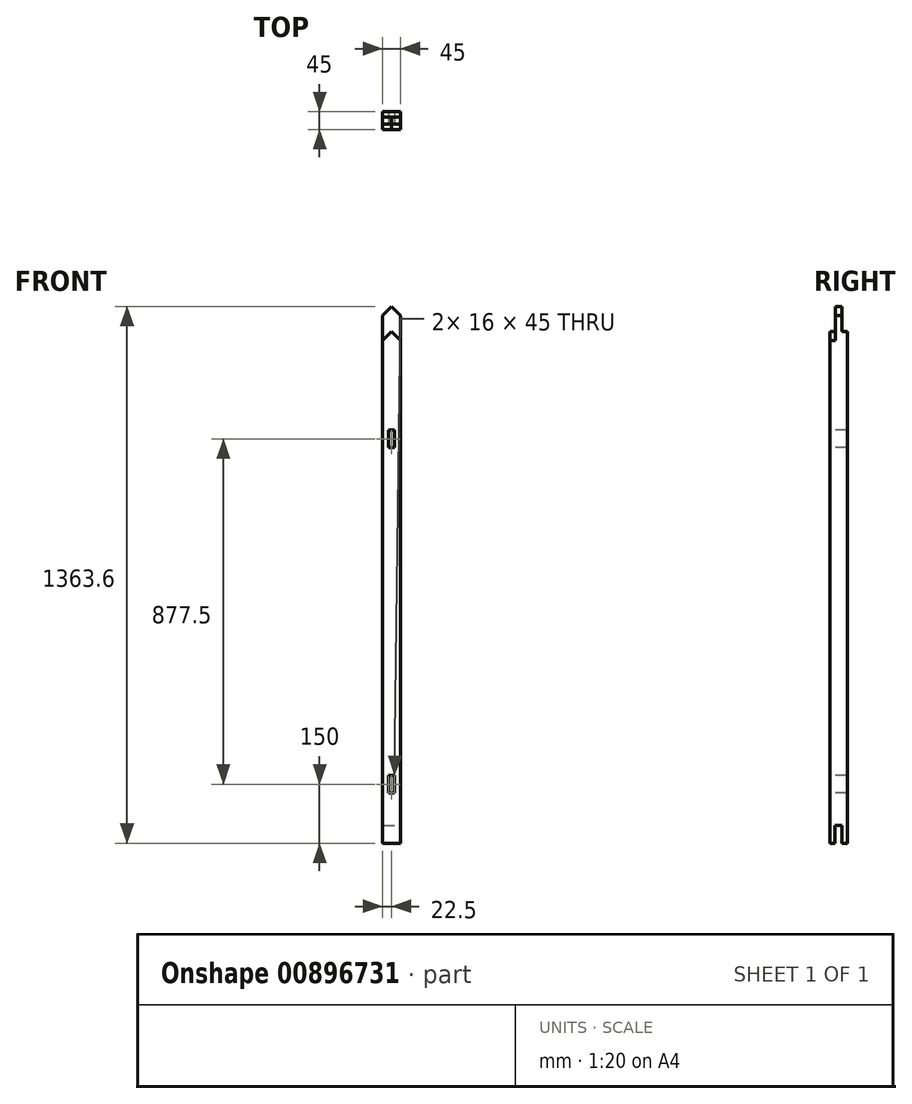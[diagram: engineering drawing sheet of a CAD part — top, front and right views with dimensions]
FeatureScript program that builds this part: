
annotation { "Feature Type Name" : "Feature", "Feature Type Description" : "" }
export const myFeature = defineFeature(function(context is Context, id is Id, definition is map)
    precondition{}
    {
        {
            var Q0;
            Q0=qCreatedBy(makeId("Top.planeOp"),FACE);
            var sketch = newSketch(context, id + "F0", { "sketchPlane" : qUnion([Q0])});
            skLineSegment(sketch, "E0.bottom", {"start": v(22.5, 22.5) * mm, "end": v(-22.5, 22.5) * mm});
            skLineSegment(sketch, "E0.top", {"start": v(22.5, -22.5) * mm, "end": v(-22.5, -22.5) * mm});
            skLineSegment(sketch, "E0.left", {"start": v(22.5, 22.5) * mm, "end": v(22.5, -22.5) * mm});
            skLineSegment(sketch, "E0.right", {"start": v(-22.5, 22.5) * mm, "end": v(-22.5, -22.5) * mm});
            skPoint(sketch, "E0.middle", {"position": v(0, 0) * mm});
            skSolve(sketch);
        }
        {
            var Q0;
            Q0 = qSketchRegion(id + "F0", true);
            extrude(context, id + "F1", {"entities" : qUnion([Q0]), "endBound" : BoundingType.SYMMETRIC, "depth" : 1300 * mm, "offsetDistance" : 25 * mm});
        }
        {
            var Q0;
            Q0=makeQuery(id+"F1.opExtrude","SWEPT_FACE",FACE,{"disambiguationData":[OSD([sQuery(id+"F0.wireOp",EDGE,"E0.top")])]});
            var sketch = newSketch(context, id + "F2", { "sketchPlane" : qUnion([Q0])});
            skLineSegment(sketch, "E1", {"start": v(0, 650) * mm, "end": v(22.5, 627.5) * mm});
            skLineSegment(sketch, "E2", {"start": v(22.5, 627.5) * mm, "end": v(22.5, 650) * mm});
            skLineSegment(sketch, "E3", {"start": v(22.5, 650) * mm, "end": v(0, 650) * mm});
            skLineSegment(sketch, "E4", {"start": v(0, 650) * mm, "end": v(-22.5, 627.5) * mm});
            skLineSegment(sketch, "E5", {"start": v(-22.5, 627.5) * mm, "end": v(-22.5, 650) * mm});
            skLineSegment(sketch, "E6", {"start": v(-22.5, 650) * mm, "end": v(0, 650) * mm});
            skSolve(sketch);
        }
        {
            var Q0;
            Q0 = qSketchRegion(id + "F2", true);
            extrude(context, id + "F3", {"entities" : qUnion([Q0]), "operationType" : NewBodyOperationType.REMOVE, "oppositeDirection" : true, "depth" : 14 * mm, "offsetDistance" : 25 * mm});
        }
        {
            var Q0;
            Q0=makeQuery(id+"F1.opExtrude","SWEPT_FACE",FACE,{"disambiguationData":[OSD([sQuery(id+"F0.wireOp",EDGE,"E0.top")])]});
            var sketch = newSketch(context, id + "F4", { "sketchPlane" : qUnion([Q0])});
            skLineSegment(sketch, "E7.bottom", {"start": v(8, -477.5) * mm, "end": v(-8, -477.5) * mm});
            skLineSegment(sketch, "E7.top", {"start": v(8, -522.5) * mm, "end": v(-8, -522.5) * mm});
            skLineSegment(sketch, "E7.left", {"start": v(8, -477.5) * mm, "end": v(8, -522.5) * mm});
            skLineSegment(sketch, "E7.right", {"start": v(-8, -477.5) * mm, "end": v(-8, -522.5) * mm});
            skPoint(sketch, "E7.middle", {"position": v(0, -500) * mm});
            skSolve(sketch);
        }
        {
            var Q0;
            Q0 = qSketchRegion(id + "F4", true);
            extrude(context, id + "F5", {"entities" : qUnion([Q0]), "operationType" : NewBodyOperationType.REMOVE, "endBound" : BoundingType.THROUGH_ALL, "oppositeDirection" : true, "depth" : 25 * mm, "offsetDistance" : 25 * mm});
        }
        {
            var Q0;
            Q0=makeQuery(id+"F1.opExtrude","SWEPT_FACE",FACE,{"disambiguationData":[OSD([sQuery(id+"F0.wireOp",EDGE,"E0.left")])]});
            var sketch = newSketch(context, id + "F6", { "sketchPlane" : qUnion([Q0])});
            skLineSegment(sketch, "E8.bottom", {"start": v(-9, -650) * mm, "end": v(9, -650) * mm});
            skLineSegment(sketch, "E8.top", {"start": v(-9, -605) * mm, "end": v(9, -605) * mm});
            skLineSegment(sketch, "E8.left", {"start": v(-9, -650) * mm, "end": v(-9, -605) * mm});
            skLineSegment(sketch, "E8.right", {"start": v(9, -650) * mm, "end": v(9, -605) * mm});
            skLineSegment(sketch, "E9", {"start": v(0, -650) * mm, "end": v(0, -543.76) * mm, "construction": true});
            skPoint(sketch, "E9.endSnap0", {"position": v(0, -650) * mm});
            skSolve(sketch);
        }
        {
            var Q0;
            Q0 = qSketchRegion(id + "F6", true);
            extrude(context, id + "F7", {"entities" : qUnion([Q0]), "operationType" : NewBodyOperationType.REMOVE, "endBound" : BoundingType.THROUGH_ALL, "oppositeDirection" : true, "depth" : 25 * mm, "offsetDistance" : 25 * mm});
        }
        {
            var Q0;
            Q0=makeQuery(id+"F1.opExtrude","SWEPT_FACE",FACE,{"disambiguationData":[OSD([sQuery(id+"F0.wireOp",EDGE,"E0.top")])]});
            var sketch = newSketch(context, id + "F8", { "sketchPlane" : qUnion([Q0])});
            skLineSegment(sketch, "E10.bottom", {"start": v(8, 400) * mm, "end": v(-8, 400) * mm});
            skLineSegment(sketch, "E10.top", {"start": v(8, 355) * mm, "end": v(-8, 355) * mm});
            skLineSegment(sketch, "E10.left", {"start": v(8, 400) * mm, "end": v(8, 355) * mm});
            skLineSegment(sketch, "E10.right", {"start": v(-8, 400) * mm, "end": v(-8, 355) * mm});
            skPoint(sketch, "E10.middle", {"position": v(0, 377.5) * mm});
            skSolve(sketch);
        }
        {
            var Q0;
            Q0 = qSketchRegion(id + "F8", true);
            extrude(context, id + "F9", {"entities" : qUnion([Q0]), "operationType" : NewBodyOperationType.REMOVE, "endBound" : BoundingType.THROUGH_ALL, "oppositeDirection" : true, "depth" : 25 * mm, "offsetDistance" : 25 * mm});
        }
        {
            var Q0;
            Q0=makeQuery(id+"F1.opExtrude","CAP_FACE",FACE,{"disambiguationData":[OSD([sQuery(id+"F0.wireOp",EDGE,"E0.bottom"),sQuery(id+"F0.wireOp",EDGE,"E0.top"),sQuery(id+"F0.wireOp",EDGE,"E0.left"),sQuery(id+"F0.wireOp",EDGE,"E0.right")])],"isStart":false});
            var sketch = newSketch(context, id + "F10", { "sketchPlane" : qUnion([Q0])});
            skLineSegment(sketch, "E11.0", {"start": v(-22.5, 8.5) * mm, "end": v(-22.5, -8.5) * mm});
            skLineSegment(sketch, "E12.0", {"start": v(22.5, 8.5) * mm, "end": v(22.5, -8.5) * mm});
            skLineSegment(sketch, "E13", {"start": v(-22.5, 8.5) * mm, "end": v(22.5, 8.5) * mm});
            skLineSegment(sketch, "E14", {"start": v(22.5, -8.5) * mm, "end": v(-22.5, -8.5) * mm});
            skSolve(sketch);
        }
        {
            var Q0;
            Q0 = qSketchRegion(id + "F10", true);
            extrude(context, id + "F11", {"entities" : qUnion([Q0]), "operationType" : NewBodyOperationType.ADD, "depth" : 63.6 * mm, "offsetDistance" : 25 * mm});
        }
        {
            var Q0;
            Q0=makeQuery(id+"F11.boolean.opBoolean","MERGE",FACE,{"derivedFrom":[makeQuery(id+"F3.boolean.opBoolean","COPY",FACE,{"derivedFrom":makeQuery(id+"F3.opExtrude","CAP_FACE",FACE,{"disambiguationData":[OSD([sQuery(id+"F2.wireOp",EDGE,"E1"),sQuery(id+"F2.wireOp",EDGE,"E2"),sQuery(id+"F2.wireOp",EDGE,"E3")])],"isStart":false})}),makeQuery(id+"F3.boolean.opBoolean","COPY",FACE,{"derivedFrom":makeQuery(id+"F3.opExtrude","CAP_FACE",FACE,{"disambiguationData":[OSD([sQuery(id+"F2.wireOp",EDGE,"E4"),sQuery(id+"F2.wireOp",EDGE,"E5"),sQuery(id+"F2.wireOp",EDGE,"E6")])],"isStart":false})}),makeQuery(id+"F11.opExtrude","SWEPT_FACE",FACE,{"disambiguationData":[OSD([sQuery(id+"F10.wireOp",EDGE,"E14")])]})]});
            var sketch = newSketch(context, id + "F12", { "sketchPlane" : qUnion([Q0])});
            skLineSegment(sketch, "E15", {"start": v(0, 713.6) * mm, "end": v(-22.5, 691.1) * mm});
            skLineSegment(sketch, "E16", {"start": v(-22.5, 691.1) * mm, "end": v(-22.5, 713.6) * mm});
            skLineSegment(sketch, "E17", {"start": v(-22.5, 713.6) * mm, "end": v(22.5, 713.6) * mm});
            skLineSegment(sketch, "E18", {"start": v(22.5, 713.6) * mm, "end": v(22.5, 691.1) * mm});
            skLineSegment(sketch, "E19", {"start": v(22.5, 691.1) * mm, "end": v(0, 713.6) * mm});
            skSolve(sketch);
        }
        {
            var Q0;
            Q0 = qSketchRegion(id + "F12", true);
            extrude(context, id + "F13", {"entities" : qUnion([Q0]), "operationType" : NewBodyOperationType.REMOVE, "endBound" : BoundingType.THROUGH_ALL, "oppositeDirection" : true, "depth" : 25 * mm, "offsetDistance" : 25 * mm});
        }
    });
